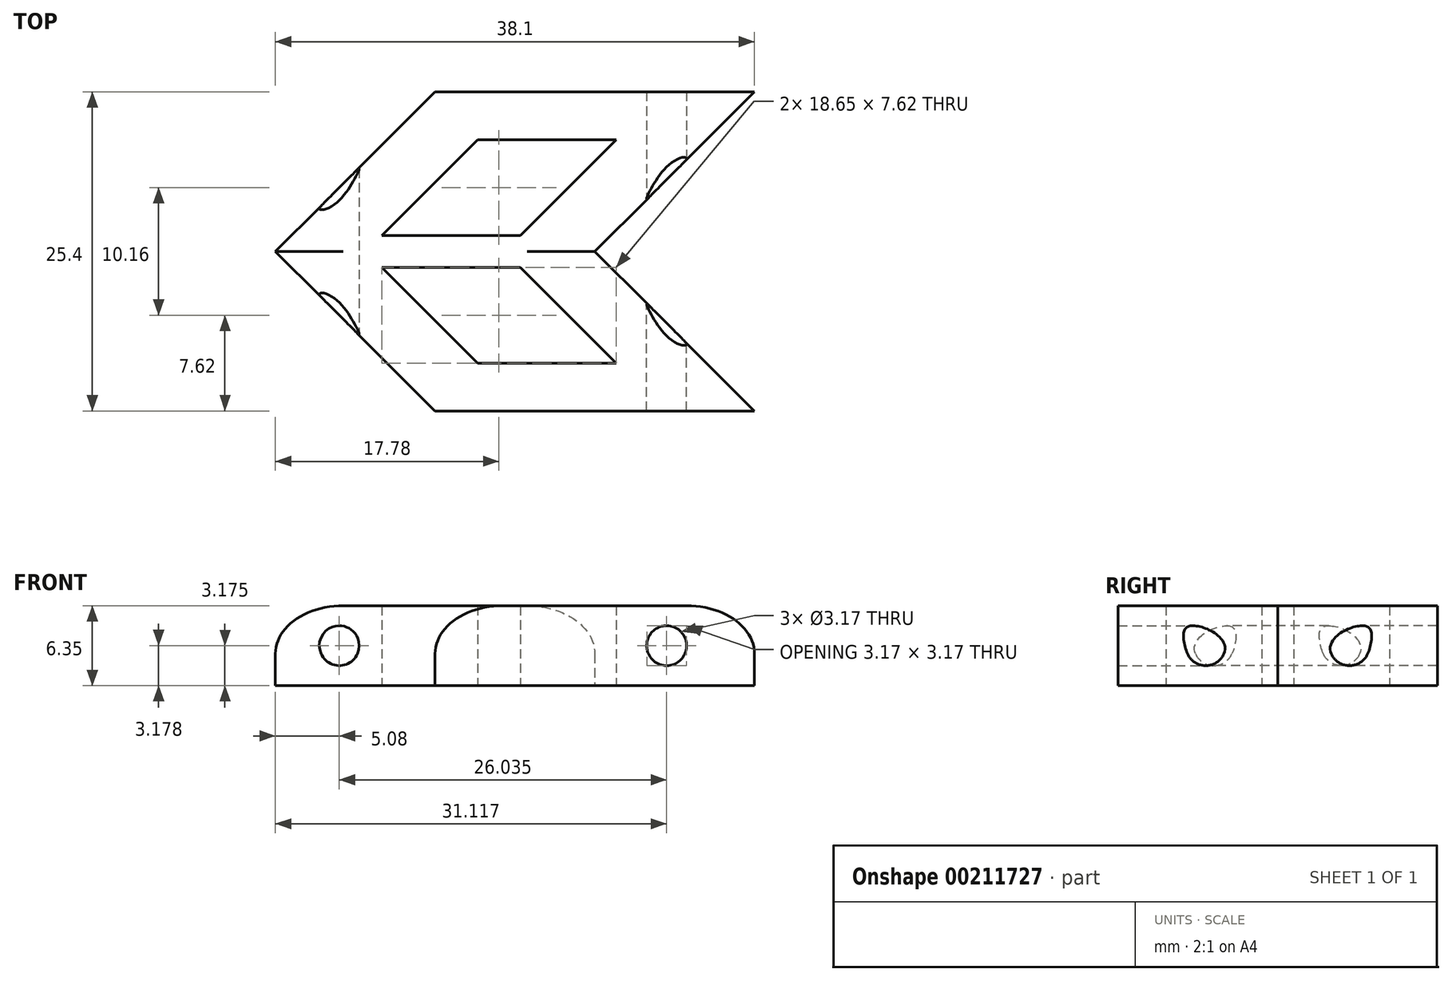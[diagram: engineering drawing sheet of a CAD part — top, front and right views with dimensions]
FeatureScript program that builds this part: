
annotation { "Feature Type Name" : "Feature", "Feature Type Description" : "" }
export const myFeature = defineFeature(function(context is Context, id is Id, definition is map)
    precondition{}
    {
        {
            var Q0;
            Q0=qCreatedBy(makeId("Top.planeOp"),FACE);
            var sketch = newSketch(context, id + "F0", { "sketchPlane" : qUnion([Q0])});
            skLineSegment(sketch, "E0", {"start": v(0, 0) * mm, "end": v(12.7, 12.7) * mm});
            skLineSegment(sketch, "E1", {"start": v(12.7, 12.7) * mm, "end": v(38.1, 12.7) * mm});
            skLineSegment(sketch, "E2", {"start": v(38.1, 12.7) * mm, "end": v(25.4, 0) * mm});
            skLineSegment(sketch, "E3", {"start": v(7.18, 0) * mm, "end": v(16.07, 8.9) * mm});
            skLineSegment(sketch, "E4", {"start": v(16.07, 8.9) * mm, "end": v(27.1, 8.9) * mm});
            skLineSegment(sketch, "E5", {"start": v(27.1, 8.9) * mm, "end": v(18.22, 0) * mm});
            skLineSegment(sketch, "E6", {"start": v(8.45, 1.27) * mm, "end": v(19.49, 1.27) * mm});
            skLineSegment(sketch, "E7", {"start": v(0, 0) * mm, "end": v(25.4, 0) * mm});
            skSolve(sketch);
        }
        {
            var Q0;
            Q0 = qSketchRegion(id + "F0", true);
            extrude(context, id + "F1", {"entities" : qUnion([Q0]), "depth" : 6.35 * mm});
        }
        {
            var Q0;
            Q0=makeQuery(id+"F1.opExtrude","SWEPT_FACE",FACE,{"disambiguationData":[OSD([sQuery(id+"F0.wireOp",EDGE,"E7")])]});
            var sketch = newSketch(context, id + "F2", { "sketchPlane" : qUnion([Q0])});
            skLineSegment(sketch, "E8.0.0", {"start": v(25.4, 0) * mm, "end": v(38.1, 0) * mm});
            skLineSegment(sketch, "E8.0.1", {"start": v(38.1, 0) * mm, "end": v(38.1, 6.35) * mm});
            skLineSegment(sketch, "E8.0.2", {"start": v(38.1, 6.35) * mm, "end": v(25.4, 6.35) * mm});
            skLineSegment(sketch, "E8.0.3", {"start": v(25.4, 6.35) * mm, "end": v(25.4, 0) * mm});
            skLineSegment(sketch, "E9", {"start": v(0, 0) * mm, "end": v(0, 6.35) * mm});
            skCircle(sketch, "E10", {"center": v(5.08, 3.18) * mm, "radius": 1.59 * mm});
            skPoint(sketch, "E10.centerSnap0", {"position": v(0, 3.18) * mm});
            skCircle(sketch, "E11", {"center": v(31.12, 3.18) * mm, "radius": 1.59 * mm});
            skPoint(sketch, "E11.centerSnap0", {"position": v(25.4, 3.18) * mm});
            skSolve(sketch);
        }
        {
            var Q0;
            Q0=makeQuery(id+"F2.imprint","IMPRINT",FACE,{"disambiguationData":[TD([[makeQuery(id+"F2.imprint","IMPRINT",EDGE,{"derivedFrom":sQuery(id+"F2.wireOp",EDGE,"E10")}),1.0]])]});
            var Q1;
            Q1=makeQuery(id+"F2.imprint","IMPRINT",FACE,{"disambiguationData":[TD([[makeQuery(id+"F2.imprint","IMPRINT",EDGE,{"derivedFrom":sQuery(id+"F2.wireOp",EDGE,"E11")}),1.0]])]});
            extrude(context, id + "F3", {"entities" : qUnion([Q0, Q1]), "operationType" : NewBodyOperationType.REMOVE, "endBound" : BoundingType.THROUGH_ALL, "oppositeDirection" : true, "depth" : 25.4 * mm});
        }
        {
            var Q0;
            Q0=makeQuery(id+"F1.opExtrude","SWEPT_BODY",BODY,{"disambiguationData":[OSD([sQuery(id+"F0.wireOp",EDGE,"E0"),sQuery(id+"F0.wireOp",EDGE,"E1"),sQuery(id+"F0.wireOp",EDGE,"E2"),sQuery(id+"F0.wireOp",EDGE,"E3"),sQuery(id+"F0.wireOp",EDGE,"E4"),sQuery(id+"F0.wireOp",EDGE,"E5"),sQuery(id+"F0.wireOp",EDGE,"E6"),sQuery(id+"F0.wireOp",EDGE,"E7")])]});
            var Q1;
            Q1=qCreatedBy(makeId("Front.planeOp"),FACE);
            mirror(context, id + "F4", {"operationType" : NewBodyOperationType.ADD, "entities" : qUnion([Q0]), "mirrorPlane" : qUnion([Q1])});
        }
        {
            var Q0;
            Q0=makeQuery(id+"F1.opExtrude","CAP_EDGE",EDGE,{"disambiguationData":[OSD([sQuery(id+"F0.wireOp",EDGE,"E2")])],"isStart":false});
            var Q1;
            Q1=makeQuery(id+"F4.opPattern","COPY",EDGE,{"derivedFrom":makeQuery(id+"F1.opExtrude","CAP_EDGE",EDGE,{"disambiguationData":[OSD([sQuery(id+"F0.wireOp",EDGE,"E2")])],"isStart":false}),"instanceName":"1"});
            var Q2;
            Q2=makeQuery(id+"F4.opPattern","COPY",EDGE,{"derivedFrom":makeQuery(id+"F1.opExtrude","CAP_EDGE",EDGE,{"disambiguationData":[OSD([sQuery(id+"F0.wireOp",EDGE,"E0")])],"isStart":false}),"instanceName":"1"});
            var Q3;
            Q3=makeQuery(id+"F1.opExtrude","CAP_EDGE",EDGE,{"disambiguationData":[OSD([sQuery(id+"F0.wireOp",EDGE,"E0")])],"isStart":false});
            fillet(context, id + "F5", {"entities" : qUnion([Q0, Q1, Q2, Q3]), "radius" : 3.8 * mm, "tangentPropagation" : true, "allowEdgeOverflow" : false});
        }
    });
